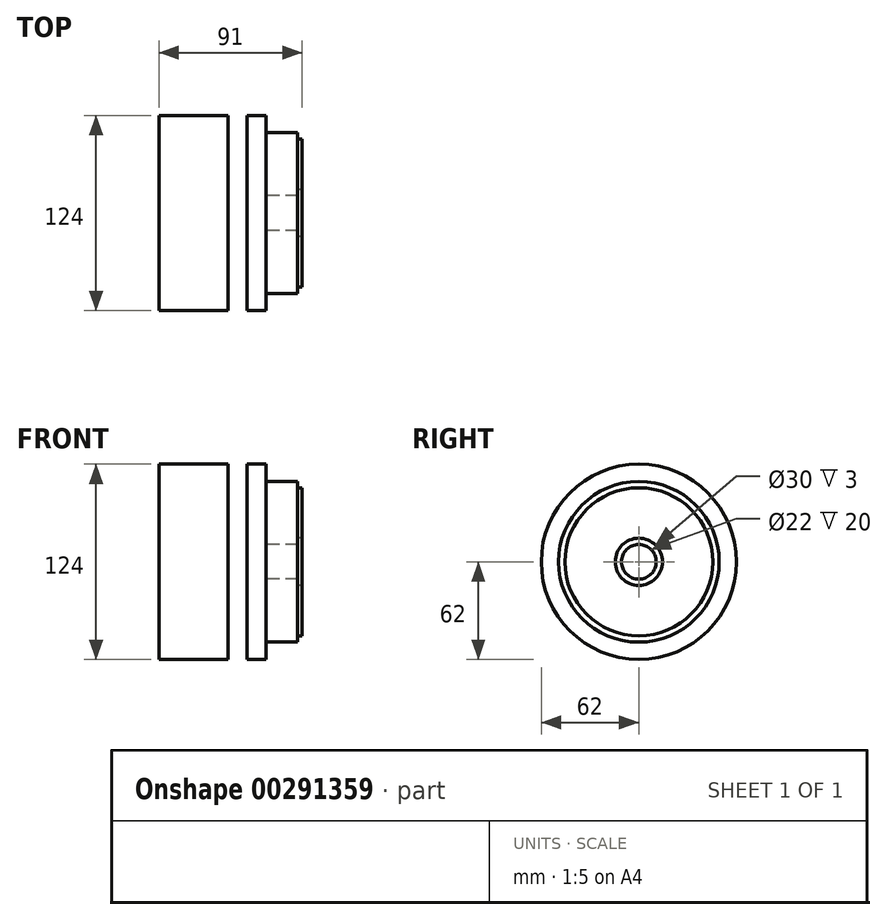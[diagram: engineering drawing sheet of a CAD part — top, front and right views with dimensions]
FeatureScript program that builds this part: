
annotation { "Feature Type Name" : "Feature", "Feature Type Description" : "" }
export const myFeature = defineFeature(function(context is Context, id is Id, definition is map)
    precondition{}
    {
        {
            var Q0;
            Q0=qCreatedBy(makeId("Front.planeOp"),FACE);
            var sketch = newSketch(context, id + "F0", { "sketchPlane" : qUnion([Q0])});
            skLineSegment(sketch, "E0.bottom", {"start": v(0, 0) * mm, "end": v(44, 0) * mm});
            skLineSegment(sketch, "E0.top", {"start": v(0, 62) * mm, "end": v(44, 62) * mm});
            skLineSegment(sketch, "E0.left", {"start": v(0, 0) * mm, "end": v(0, 62) * mm});
            skArc(sketch, "E1", {"start": v(56, 62) * mm, "mid": v(50, 56) * mm, "end": v(44, 62) * mm});
            skArc(sketch, "E2", {"start": v(56, 0) * mm, "mid": v(50, 6) * mm, "end": v(44, 0) * mm});
            skLineSegment(sketch, "E3.bottom", {"start": v(56, 62) * mm, "end": v(68, 62) * mm});
            skLineSegment(sketch, "E3.top", {"start": v(56, 0) * mm, "end": v(68, 0) * mm});
            skLineSegment(sketch, "E3.left", {"start": v(56, 62) * mm, "end": v(56, 0) * mm});
            skLineSegment(sketch, "E3.right", {"start": v(68, 62) * mm, "end": v(68, 0) * mm});
            skLineSegment(sketch, "E4", {"start": v(44, 62) * mm, "end": v(44, 0) * mm});
            skLineSegment(sketch, "E5.bottom", {"start": v(88, 51) * mm, "end": v(68, 51) * mm});
            skLineSegment(sketch, "E5.top", {"start": v(88, 11) * mm, "end": v(68, 11) * mm});
            skLineSegment(sketch, "E5.left", {"start": v(88, 51) * mm, "end": v(88, 11) * mm});
            skPoint(sketch, "E5.middle", {"position": v(68, 31) * mm});
            skPoint(sketch, "E5.right.start.orphan", {"position": v(48, 51) * mm});
            skPoint(sketch, "E6.orphan", {"position": v(48, 11) * mm});
            skLineSegment(sketch, "E7.bottom", {"start": v(91, 47) * mm, "end": v(88, 47) * mm});
            skLineSegment(sketch, "E7.top", {"start": v(91, 15) * mm, "end": v(88, 15) * mm});
            skLineSegment(sketch, "E7.left", {"start": v(91, 47) * mm, "end": v(91, 15) * mm});
            skPoint(sketch, "E7.middle", {"position": v(88, 31) * mm});
            skPoint(sketch, "E7.right.start.orphan", {"position": v(85, 47) * mm});
            skPoint(sketch, "E8.orphan", {"position": v(85, 15) * mm});
            skSolve(sketch);
        }
        {
            var Q0;
            Q0=makeQuery(id+"F0.imprint","IMPRINT",FACE,{"disambiguationData":[TD([[makeQuery(id+"F0.imprint","IMPRINT",EDGE,{"derivedFrom":sQuery(id+"F0.wireOp",EDGE,"E0.bottom")}),1.0]])]});
            var Q1;
            Q1=makeQuery(id+"F0.imprint","IMPRINT",FACE,{"disambiguationData":[TD([[makeQuery(id+"F0.imprint","IMPRINT",EDGE,{"derivedFrom":sQuery(id+"F0.wireOp",EDGE,"E1")}),1.0]])]});
            var Q2;
            {var subQ1=sQuery(id+"F0.wireOp",EDGE,"E3.bottom");Q2=makeQuery(id+"F0.imprint","IMPRINT",FACE,{"disambiguationData":[TD([[makeQuery(id+"F0.imprint","IMPRINT",EDGE,{"derivedFrom":subQ1}),-1.0]])]});}
            var Q3;
            {var subQ1=sQuery(id+"F0.wireOp",EDGE,"E5.bottom");Q3=makeQuery(id+"F0.imprint","IMPRINT",FACE,{"disambiguationData":[TD([[makeQuery(id+"F0.imprint","IMPRINT",EDGE,{"derivedFrom":subQ1}),1.0]])]});}
            var Q4;
            {var subQ0=sQuery(id+"F0.wireOp",EDGE,"E7.bottom");Q4=makeQuery(id+"F0.imprint","IMPRINT",FACE,{"disambiguationData":[TD([[makeQuery(id+"F0.imprint","IMPRINT",EDGE,{"derivedFrom":subQ0}),1.0]])]});}
            var Q5;
            Q5=sQuery(id+"F0.wireOp",EDGE,"E3.bottom");
            revolve(context, id + "F1", {"entities" : qUnion([Q0, Q1, Q2, Q3, Q4]), "axis" : qUnion([Q5]), "revolveType" : RevolveType.FULL});
        }
    });
